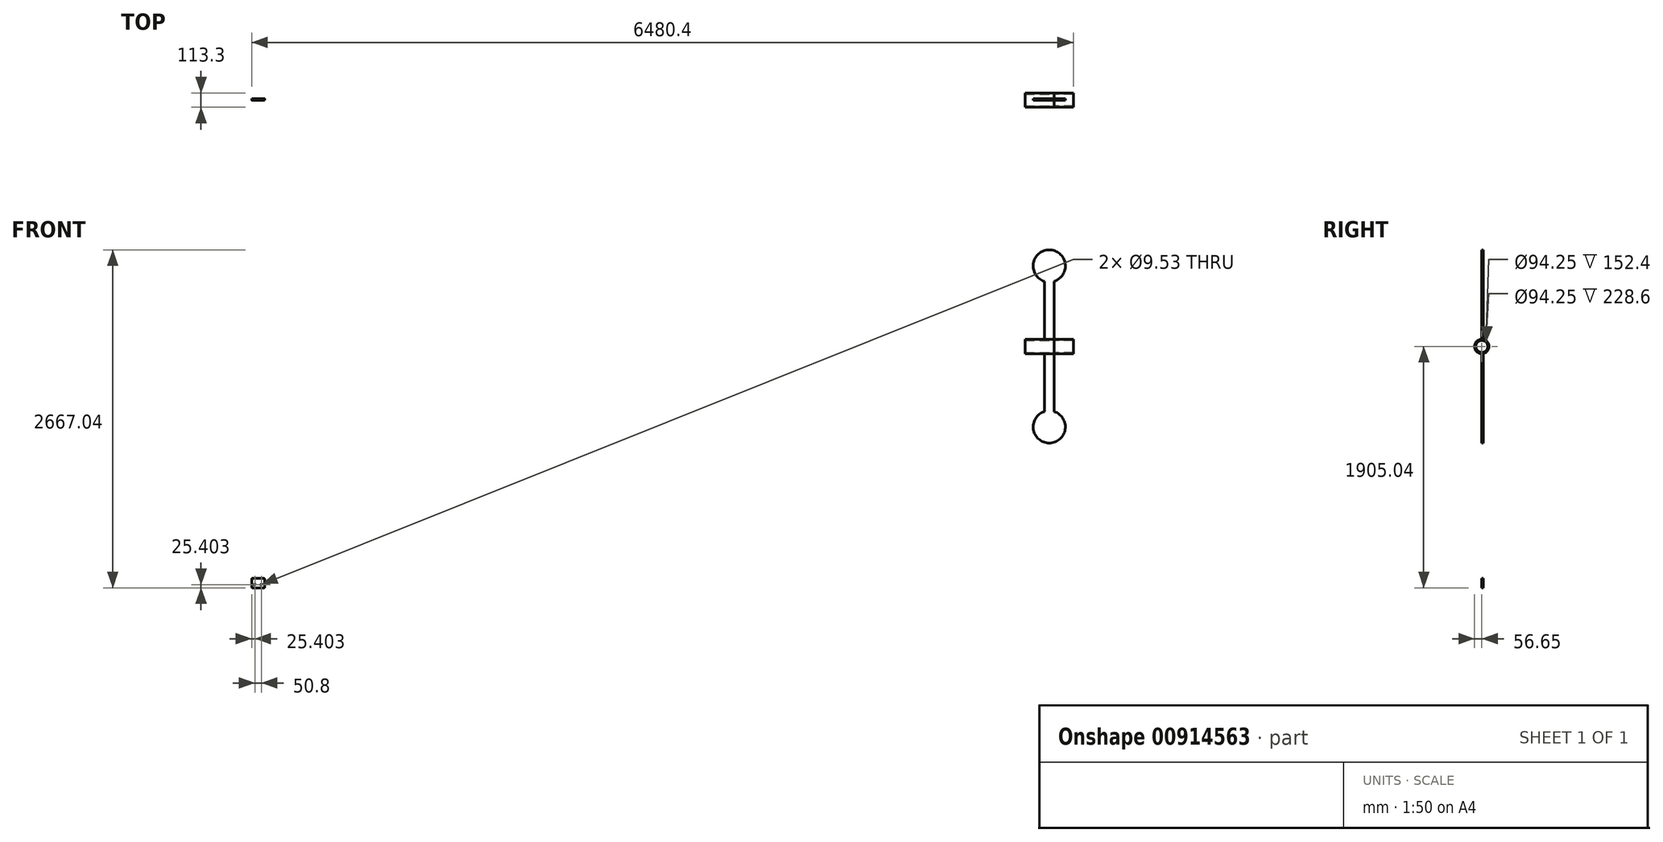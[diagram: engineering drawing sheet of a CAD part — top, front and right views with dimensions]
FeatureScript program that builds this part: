
annotation { "Feature Type Name" : "Feature", "Feature Type Description" : "" }
export const myFeature = defineFeature(function(context is Context, id is Id, definition is map)
    precondition{}
    {
        {
            var Q0;
            Q0=qCreatedBy(makeId("Front.planeOp"),FACE);
            var sketch = newSketch(context, id + "F0", { "sketchPlane" : qUnion([Q0])});
            skArc(sketch, "E0", {"start": v(-868.38, -111.44) * mm, "mid": v(-906.48, 136.71) * mm, "end": v(-944.58, -111.44) * mm});
            skArc(sketch, "E1", {"start": v(-944.58, -1139.14) * mm, "mid": v(-906.48, -1387.29) * mm, "end": v(-868.38, -1139.14) * mm});
            skLineSegment(sketch, "E2.top", {"start": v(-944.58, -568.64) * mm, "end": v(-868.38, -568.64) * mm});
            skLineSegment(sketch, "E2.left", {"start": v(-944.58, -111.44) * mm, "end": v(-944.58, -568.64) * mm});
            skLineSegment(sketch, "E2.right", {"start": v(-868.38, -111.44) * mm, "end": v(-868.38, -568.64) * mm});
            skLineSegment(sketch, "E3.top", {"start": v(-944.58, -681.94) * mm, "end": v(-868.38, -681.94) * mm});
            skLineSegment(sketch, "E3.left", {"start": v(-944.58, -1139.14) * mm, "end": v(-944.58, -681.94) * mm});
            skLineSegment(sketch, "E3.right", {"start": v(-868.38, -1139.14) * mm, "end": v(-868.38, -681.94) * mm});
            skPoint(sketch, "E4", {"position": v(-906.48, -681.94) * mm});
            skPoint(sketch, "E5", {"position": v(-906.48, -568.64) * mm});
            skLineSegment(sketch, "E6.bottom", {"start": v(-7190.03, -2454.13) * mm, "end": v(-7101.13, -2454.13) * mm});
            skLineSegment(sketch, "E6.top", {"start": v(-7190.03, -2530.33) * mm, "end": v(-7101.13, -2530.33) * mm});
            skLineSegment(sketch, "E6.left", {"start": v(-7196.38, -2460.48) * mm, "end": v(-7196.38, -2523.98) * mm});
            skLineSegment(sketch, "E6.right", {"start": v(-7094.78, -2460.48) * mm, "end": v(-7094.78, -2523.98) * mm});
            skCircle(sketch, "E7", {"center": v(-7120.18, -2504.93) * mm, "radius": 4.76 * mm});
            skCircle(sketch, "E8", {"center": v(-7170.98, -2504.93) * mm, "radius": 4.76 * mm});
            skPoint(sketch, "E9.visualSharp", {"position": v(-7094.78, -2530.33) * mm});
            skArc(sketch, "E9.filletArc", {"start": v(-7101.13, -2530.33) * mm, "mid": v(-7096.64, -2528.47) * mm, "end": v(-7094.78, -2523.98) * mm});
            skPoint(sketch, "E10.visualSharp", {"position": v(-7196.38, -2530.33) * mm});
            skArc(sketch, "E10.filletArc", {"start": v(-7196.38, -2523.98) * mm, "mid": v(-7194.52, -2528.47) * mm, "end": v(-7190.03, -2530.33) * mm});
            skPoint(sketch, "E11.visualSharp", {"position": v(-7196.38, -2454.13) * mm});
            skArc(sketch, "E11.filletArc", {"start": v(-7190.03, -2454.13) * mm, "mid": v(-7194.52, -2455.99) * mm, "end": v(-7196.38, -2460.48) * mm});
            skPoint(sketch, "E12.visualSharp", {"position": v(-7094.78, -2454.13) * mm});
            skArc(sketch, "E12.filletArc", {"start": v(-7094.78, -2460.48) * mm, "mid": v(-7096.64, -2455.99) * mm, "end": v(-7101.13, -2454.13) * mm});
            skSolve(sketch);
        }
        {
            var Q0;
            {var subQ0=sQuery(id+"F0.wireOp",EDGE,"E2.bottom");Q0=makeQuery(id+"F0.imprint","IMPRINT",FACE,{"disambiguationData":[TD([[makeQuery(id+"F0.imprint","IMPRINT",EDGE,{"derivedFrom":subQ0}),1.0]])]});}
            var Q1;
            Q1=makeQuery(id+"F0.imprint","IMPRINT",FACE,{"disambiguationData":[TD([[makeQuery(id+"F0.imprint","IMPRINT",EDGE,{"derivedFrom":sQuery(id+"F0.wireOp",EDGE,"E2.top")}),1.0]])]});
            var Q2;
            Q2=makeQuery(id+"F0.imprint","IMPRINT",FACE,{"disambiguationData":[TD([[makeQuery(id+"F0.imprint","IMPRINT",EDGE,{"derivedFrom":sQuery(id+"F0.wireOp",EDGE,"E3.top")}),-1.0]])]});
            var Q3;
            {var subQ0=sQuery(id+"F0.wireOp",EDGE,"E3.bottom");Q3=makeQuery(id+"F0.imprint","IMPRINT",FACE,{"disambiguationData":[TD([[makeQuery(id+"F0.imprint","IMPRINT",EDGE,{"derivedFrom":subQ0}),-1.0]])]});}
            var Q4;
            Q4=makeQuery(id+"F0.imprint","IMPRINT",FACE,{"disambiguationData":[TD([[makeQuery(id+"F0.imprint","IMPRINT",EDGE,{"derivedFrom":sQuery(id+"F0.wireOp",EDGE,"E6.bottom")}),-1.0]])]});
            extrude(context, id + "F1", {"entities" : qUnion([Q0, Q1, Q2, Q3, Q4]), "depth" : 12.7 * mm, "offsetDistance" : 25.4 * mm});
        }
        {
            var Q0;
            Q0=makeQuery(id+"F1.opExtrude","SWEPT_FACE",FACE,{"disambiguationData":[OSD([sQuery(id+"F0.wireOp",EDGE,"E2.right")])]});
            var sketch = newSketch(context, id + "F2", { "sketchPlane" : qUnion([Q0])});
            skCircle(sketch, "E13", {"center": v(-12.79, -625.29) * mm, "radius": 56.65 * mm});
            skCircle(sketch, "E14", {"center": v(-12.79, -625.29) * mm, "radius": 47.12 * mm});
            skSolve(sketch);
        }
        {
            var Q0;
            Q0=makeQuery(id+"F2.imprint","IMPRINT",FACE,{"disambiguationData":[TD([[makeQuery(id+"F2.imprint","IMPRINT",EDGE,{"derivedFrom":sQuery(id+"F2.wireOp",EDGE,"E13")}),1.0]])]});
            extrude(context, id + "F3", {"entities" : qUnion([Q0]), "depth" : 152.4 * mm, "offsetDistance" : 25.4 * mm});
        }
        {
            var Q0;
            Q0=makeQuery(id+"F3.opExtrude","CAP_FACE",FACE,{"disambiguationData":[OSD([sQuery(id+"F2.wireOp",EDGE,"E13"),sQuery(id+"F2.wireOp",EDGE,"E14")])],"isStart":true});
            extrude(context, id + "F4", {"entities" : qUnion([Q0]), "depth" : 228.6 * mm, "offsetDistance" : 25.4 * mm});
        }
    });
